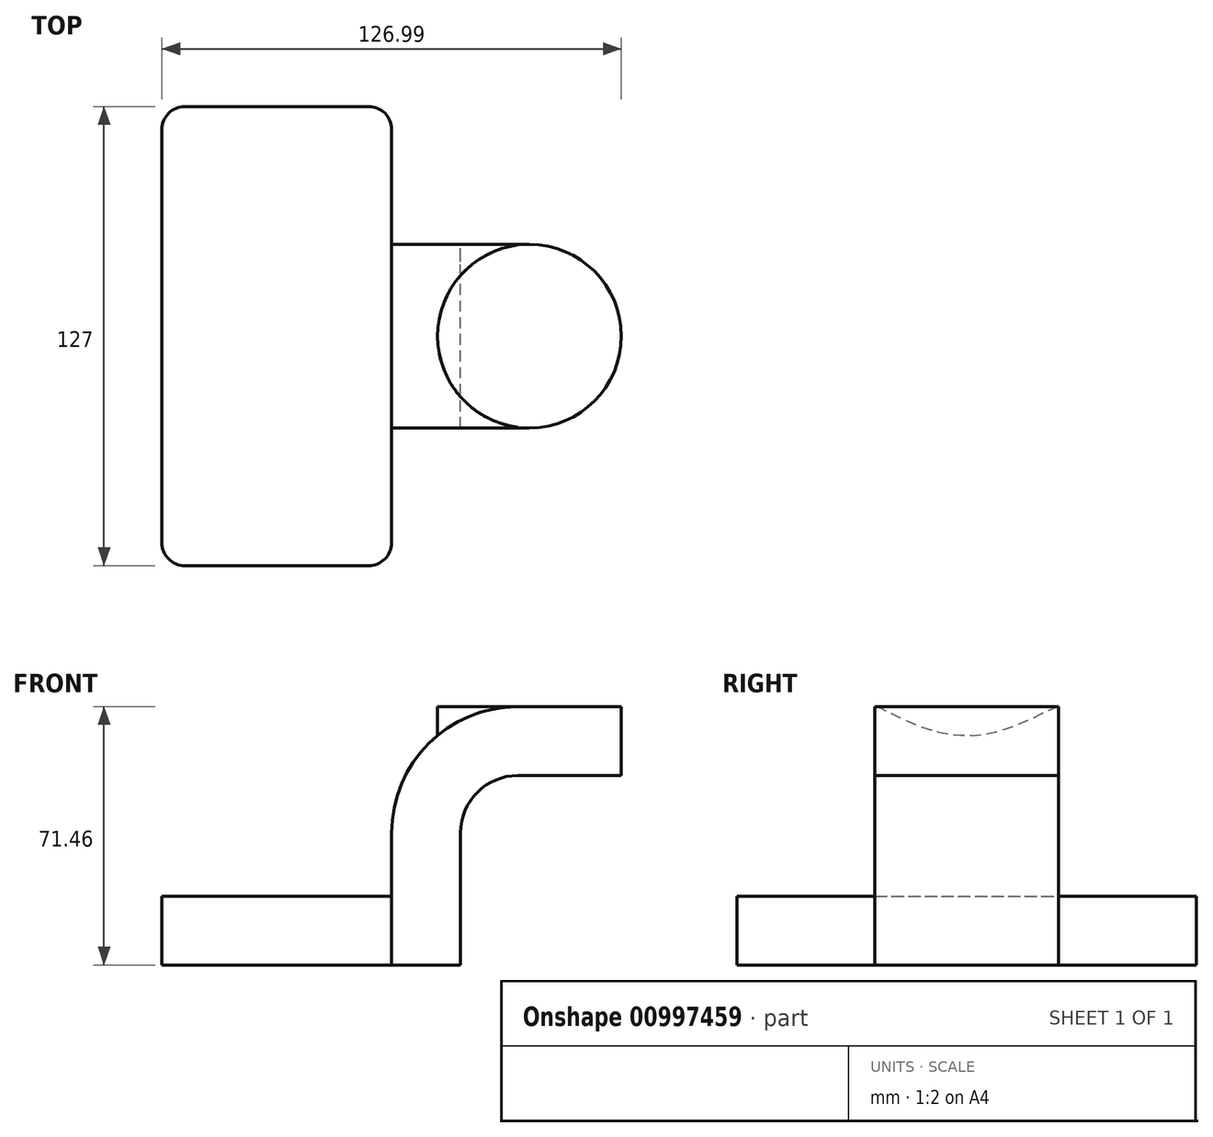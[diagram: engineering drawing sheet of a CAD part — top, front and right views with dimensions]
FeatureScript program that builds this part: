
annotation { "Feature Type Name" : "Feature", "Feature Type Description" : "" }
export const myFeature = defineFeature(function(context is Context, id is Id, definition is map)
    precondition{}
    {
        {
            var Q0;
            Q0=qCreatedBy(makeId("Front.planeOp"),FACE);
            var sketch = newSketch(context, id + "F0", { "sketchPlane" : qUnion([Q0])});
            skLineSegment(sketch, "E0.bottom", {"start": v(41.28, -9.52) * mm, "end": v(-41.28, -9.52) * mm});
            skLineSegment(sketch, "E0.top", {"start": v(41.28, 9.53) * mm, "end": v(-41.28, 9.53) * mm});
            skLineSegment(sketch, "E0.left", {"start": v(41.28, -9.52) * mm, "end": v(41.28, 9.53) * mm});
            skLineSegment(sketch, "E0.right", {"start": v(-41.28, -9.52) * mm, "end": v(-41.28, 9.53) * mm});
            skPoint(sketch, "E0.middle", {"position": v(0, 0) * mm});
            skLineSegment(sketch, "E1.bottom", {"start": v(111.12, 38.1) * mm, "end": v(60.33, 38.1) * mm});
            skLineSegment(sketch, "E1.top", {"start": v(111.12, 66.68) * mm, "end": v(60.33, 66.68) * mm});
            skLineSegment(sketch, "E1.left", {"start": v(111.13, 38.1) * mm, "end": v(111.13, 66.68) * mm});
            skLineSegment(sketch, "E1.right", {"start": v(60.33, 38.1) * mm, "end": v(60.33, 66.68) * mm});
            skPoint(sketch, "E1.middle", {"position": v(85.73, 52.39) * mm});
            skLineSegment(sketch, "E2", {"start": v(41.28, 9.53) * mm, "end": v(41.28, 27) * mm});
            skArc(sketch, "E3", {"start": v(41.27, 27) * mm, "mid": v(45.92, 38.23) * mm, "end": v(57.15, 42.88) * mm});
            skLineSegment(sketch, "E4", {"start": v(57.15, 42.88) * mm, "end": v(85.73, 42.88) * mm});
            skArc(sketch, "E5.0", {"start": v(22.23, 27) * mm, "mid": v(32.45, 51.7) * mm, "end": v(57.15, 61.93) * mm});
            skLineSegment(sketch, "E5.1", {"start": v(22.23, -11.69) * mm, "end": v(22.23, 27) * mm});
            skLineSegment(sketch, "E6", {"start": v(57.15, 61.93) * mm, "end": v(85.73, 61.93) * mm});
            skLineSegment(sketch, "E7", {"start": v(85.73, 38.1) * mm, "end": v(85.73, 66.68) * mm});
            skFitSpline(sketch, "E8", {"points": [v(-41.28, 9.53) * mm, v(57.15, 61.93) * mm], "startDerivative": vector(0, 117.15) * mm, "endDerivative": vector(112.24, 0) * mm});
            skFitSpline(sketch, "E9", {"points": [v(57.17, 61.93) * mm, v(56.65, 61.93) * mm], "startDerivative": vector(-0.52, 0) * mm, "endDerivative": vector(-0.52, 0) * mm});
            skSolve(sketch);
        }
        {
            var Q0;
            {var subQ0=sQuery(id+"F0.wireOp",EDGE,"E0.right");Q0=makeQuery(id+"F0.imprint","IMPRINT",FACE,{"disambiguationData":[TD([[makeQuery(id+"F0.imprint","IMPRINT",EDGE,{"derivedFrom":subQ0}),-1.0]])]});}
            extrude(context, id + "F1", {"entities" : qUnion([Q0]), "endBound" : BoundingType.SYMMETRIC, "depth" : 127 * mm, "offsetDistance" : 25.4 * mm});
        }
        {
            var Q0;
            {var subQ0=sQuery(id+"F0.wireOp",EDGE,"E0.left");Q0=makeQuery(id+"F0.imprint","IMPRINT",FACE,{"disambiguationData":[TD([[makeQuery(id+"F0.imprint","IMPRINT",EDGE,{"derivedFrom":subQ0}),1.0]])]});}
            var Q1;
            {var subQ1=sQuery(id+"F0.wireOp",EDGE,"E2");Q1=makeQuery(id+"F0.imprint","IMPRINT",FACE,{"disambiguationData":[TD([[makeQuery(id+"F0.imprint","IMPRINT",EDGE,{"derivedFrom":subQ1}),1.0]])]});}
            extrude(context, id + "F2", {"entities" : qUnion([Q0, Q1]), "operationType" : NewBodyOperationType.ADD, "endBound" : BoundingType.SYMMETRIC, "depth" : 50.8 * mm, "offsetDistance" : 25.4 * mm});
        }
        {
            var Q0;
            {var subQ4=sQuery(id+"F0.wireOp",EDGE,"E5.0");Q0=makeQuery(id+"F0.imprint","IMPRINT",FACE,{"disambiguationData":[TD([[makeQuery(id+"F0.imprint","IMPRINT",EDGE,{"derivedFrom":subQ4}),1.0]])]});}
            extrude(context, id + "F3", {"entities" : qUnion([Q0]), "operationType" : NewBodyOperationType.ADD, "depth" : 15.88 * mm, "offsetDistance" : 25.4 * mm});
        }
        {
            var Q0;
            {var subQ0=sQuery(id+"F0.wireOp",EDGE,"E4");var subQ1=sQuery(id+"F0.wireOp",EDGE,"E1.right");var subQ2=makeQuery(id+"F0.imprint","INTERSECT",VERTEX,{"derivedFrom":[subQ1,subQ0]});Q0=makeQuery(id+"F0.imprint","IMPRINT",FACE,{"disambiguationData":[TD([[makeQuery(id+"F0.imprint","IMPRINT",EDGE,{"disambiguationData":[TD([[subQ2,-1.0]])],"derivedFrom":subQ1}),-1.0]])]});}
            var Q1;
            Q1=sQuery(id+"F0.wireOp",EDGE,"E1.right");
            revolve(context, id + "F4", {"operationType" : NewBodyOperationType.ADD, "surfaceOperationType" : NewSurfaceOperationType.NEW, "entities" : qUnion([Q0]), "axis" : qUnion([Q1]), "revolveType" : RevolveType.FULL});
        }
        {
            var Q0;
            Q0=makeQuery(id+"F1.opExtrude","CAP_EDGE",EDGE,{"disambiguationData":[OSD([sQuery(id+"F0.wireOp",EDGE,"E0.right")])],"isStart":false});
            var Q1;
            Q1=makeQuery(id+"F1.opExtrude","CAP_EDGE",EDGE,{"disambiguationData":[OSD([sQuery(id+"F0.wireOp",EDGE,"E5.1")])],"isStart":false});
            var Q2;
            Q2=makeQuery(id+"F1.opExtrude","CAP_EDGE",EDGE,{"disambiguationData":[OSD([sQuery(id+"F0.wireOp",EDGE,"E0.right")])],"isStart":true});
            var Q3;
            Q3=makeQuery(id+"F1.opExtrude","CAP_EDGE",EDGE,{"disambiguationData":[OSD([sQuery(id+"F0.wireOp",EDGE,"E5.1")])],"isStart":true});
            fillet(context, id + "F5", {"entities" : qUnion([Q0, Q1, Q2, Q3]), "radius" : 6.35 * mm, "tangentPropagation" : true, "allowEdgeOverflow" : false});
        }
    });
